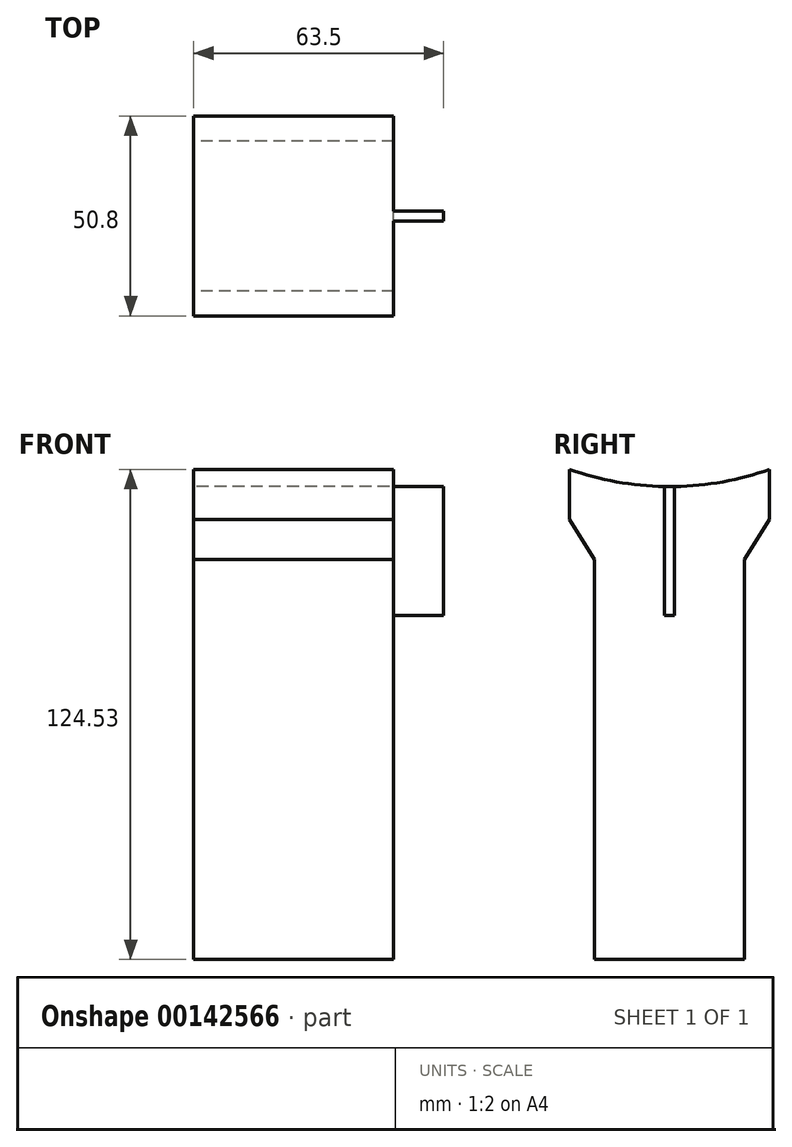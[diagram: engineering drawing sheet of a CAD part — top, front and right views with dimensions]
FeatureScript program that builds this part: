
annotation { "Feature Type Name" : "Feature", "Feature Type Description" : "" }
export const myFeature = defineFeature(function(context is Context, id is Id, definition is map)
    precondition{}
    {
        {
            var Q0;
            Q0=qCreatedBy(makeId("Right.planeOp"),FACE);
            var sketch = newSketch(context, id + "F0", { "sketchPlane" : qUnion([Q0])});
            skArc(sketch, "E0", {"start": v(-25.4, 0) * mm, "mid": v(0, -4.36) * mm, "end": v(25.4, 0) * mm});
            skLineSegment(sketch, "E1", {"start": v(-25.4, 0) * mm, "end": v(-25.4, -12.7) * mm});
            skLineSegment(sketch, "E2", {"start": v(-25.4, -12.7) * mm, "end": v(-19.05, -22.93) * mm});
            skLineSegment(sketch, "E3", {"start": v(-19.05, -22.93) * mm, "end": v(-19.05, -124.53) * mm});
            skLineSegment(sketch, "E4", {"start": v(-19.05, -124.53) * mm, "end": v(19.05, -124.53) * mm});
            skLineSegment(sketch, "E5", {"start": v(19.05, -124.53) * mm, "end": v(19.05, -22.93) * mm});
            skLineSegment(sketch, "E6", {"start": v(19.05, -22.93) * mm, "end": v(25.4, -12.7) * mm});
            skLineSegment(sketch, "E7", {"start": v(25.4, -12.7) * mm, "end": v(25.4, 0) * mm});
            skSolve(sketch);
        }
        {
            var Q0;
            Q0 = qSketchRegion(id + "F0", true);
            extrude(context, id + "F1", {"entities" : qUnion([Q0]), "depth" : 50.8 * mm});
        }
        {
            var Q0;
            Q0=makeQuery(id+"F1.opExtrude","CAP_FACE",FACE,{"disambiguationData":[OSD([sQuery(id+"F0.wireOp",EDGE,"E0"),sQuery(id+"F0.wireOp",EDGE,"E1"),sQuery(id+"F0.wireOp",EDGE,"E2"),sQuery(id+"F0.wireOp",EDGE,"E3"),sQuery(id+"F0.wireOp",EDGE,"E4"),sQuery(id+"F0.wireOp",EDGE,"E5"),sQuery(id+"F0.wireOp",EDGE,"E6"),sQuery(id+"F0.wireOp",EDGE,"E7")])],"isStart":false});
            var sketch = newSketch(context, id + "F2", { "sketchPlane" : qUnion([Q0])});
            skLineSegment(sketch, "E8", {"start": v(-1.27, -4.35) * mm, "end": v(-1.27, -37.16) * mm});
            skLineSegment(sketch, "E9", {"start": v(-1.27, -37.16) * mm, "end": v(1.27, -37.16) * mm});
            skLineSegment(sketch, "E10", {"start": v(1.27, -37.16) * mm, "end": v(1.27, -4.35) * mm});
            skSolve(sketch);
        }
        {
            var Q0;
            Q0 = qSketchRegion(id + "F2", true);
            var Q1;
            {var subQ0=sQuery(id+"F2.wireOp",EDGE,"E8");Q1=makeQuery(id+"F2.imprint","IMPRINT",FACE,{"disambiguationData":[TD([[makeQuery(id+"F2.imprint","IMPRINT",EDGE,{"derivedFrom":subQ0}),1.0]])]});}
            extrude(context, id + "F3", {"entities" : qUnion([Q0, Q1]), "operationType" : NewBodyOperationType.ADD, "depth" : 12.7 * mm});
        }
    });
